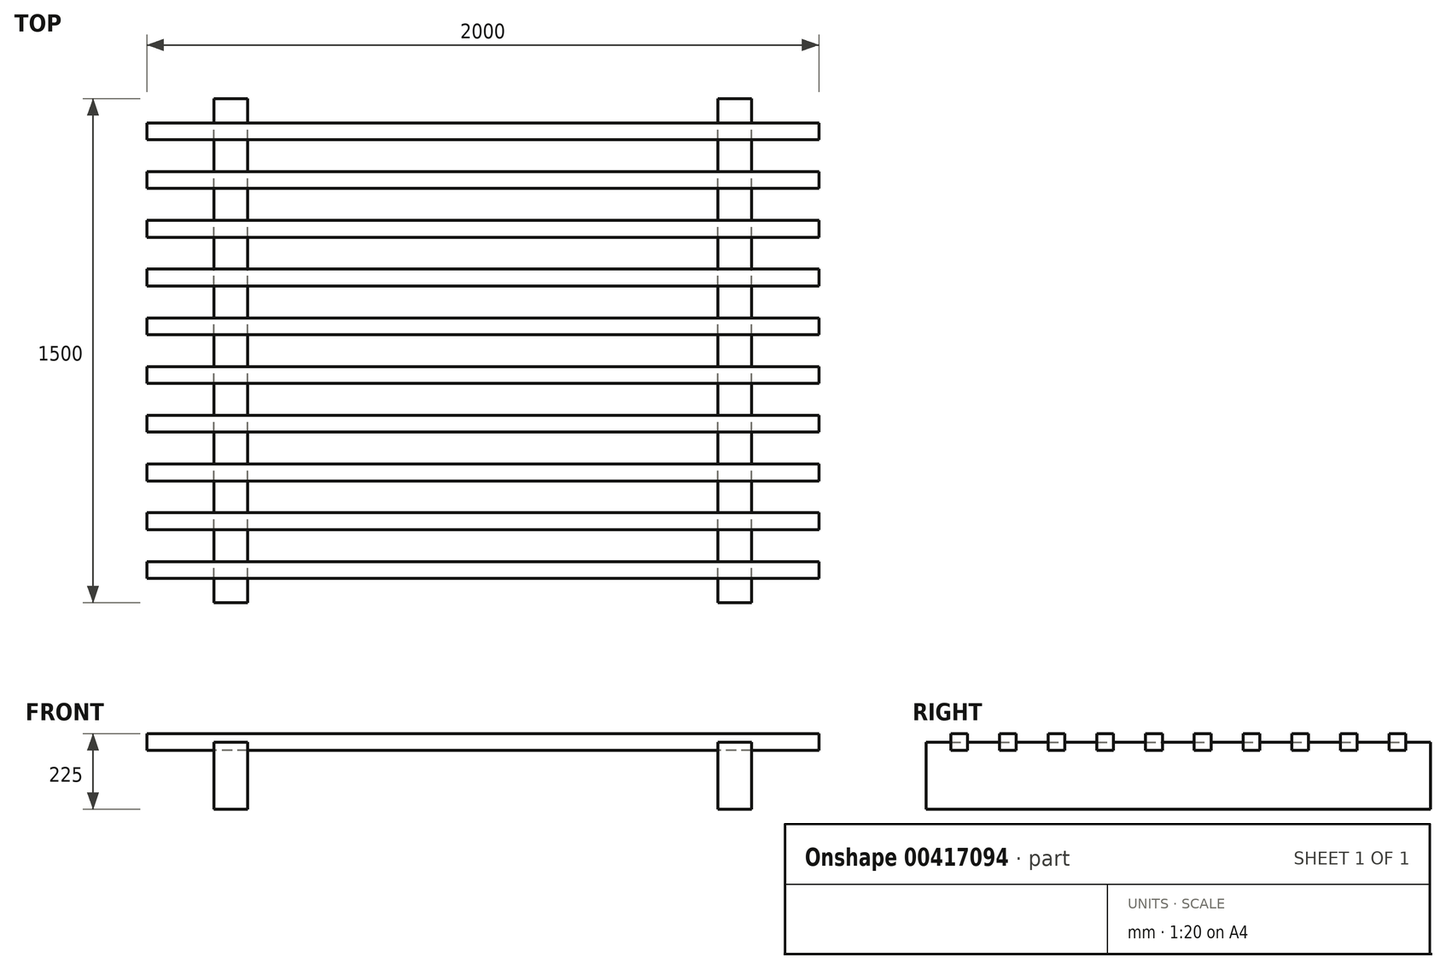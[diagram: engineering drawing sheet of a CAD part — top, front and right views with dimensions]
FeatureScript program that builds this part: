
annotation { "Feature Type Name" : "Feature", "Feature Type Description" : "" }
export const myFeature = defineFeature(function(context is Context, id is Id, definition is map)
    precondition{}
    {
        {
            var Q0;
            Q0=qCreatedBy(makeId("Top.planeOp"),FACE);
            var sketch = newSketch(context, id + "F0", { "sketchPlane" : qUnion([Q0])});
            skLineSegment(sketch, "E0.bottom", {"start": v(0, 0) * mm, "end": v(100, 0) * mm});
            skLineSegment(sketch, "E0.top", {"start": v(0, 1500) * mm, "end": v(100, 1500) * mm});
            skLineSegment(sketch, "E0.left", {"start": v(0, 0) * mm, "end": v(0, 1500) * mm});
            skLineSegment(sketch, "E0.right", {"start": v(100, 0) * mm, "end": v(100, 1500) * mm});
            skLineSegment(sketch, "E1.bottom", {"start": v(1500, 0) * mm, "end": v(1600, 0) * mm});
            skLineSegment(sketch, "E1.top", {"start": v(1500, 1500) * mm, "end": v(1600, 1500) * mm});
            skLineSegment(sketch, "E1.left", {"start": v(1500, 0) * mm, "end": v(1500, 1500) * mm});
            skLineSegment(sketch, "E1.right", {"start": v(1600, 0) * mm, "end": v(1600, 1500) * mm});
            skSolve(sketch);
        }
        {
            var Q0;
            Q0 = qSketchRegion(id + "F0", true);
            extrude(context, id + "F1", {"entities" : qUnion([Q0]), "depth" : 200 * mm});
        }
        {
            var Q0;
            Q0=makeQuery(id+"F1.opExtrude","SWEPT_FACE",FACE,{"disambiguationData":[OSD([sQuery(id+"F0.wireOp",EDGE,"E0.left")])]});
            cPlane(context, id + "F2", {"entities" : qUnion([Q0]), "cplaneType" : CPlaneType.OFFSET, "offset" : 200 * mm, "width" : 150 * mm, "height" : 150 * mm});
        }
        {
            var Q0;
            Q0=qCreatedBy(id+"F2.planeOp",FACE);
            var sketch = newSketch(context, id + "F3", { "sketchPlane" : qUnion([Q0])});
            skLineSegment(sketch, "E2.bottom", {"start": v(-1427.5, 225) * mm, "end": v(-1377.5, 225) * mm});
            skLineSegment(sketch, "E2.top", {"start": v(-1427.5, 175) * mm, "end": v(-1377.5, 175) * mm});
            skLineSegment(sketch, "E2.left", {"start": v(-1427.5, 225) * mm, "end": v(-1427.5, 175) * mm});
            skLineSegment(sketch, "E2.right", {"start": v(-1377.5, 225) * mm, "end": v(-1377.5, 175) * mm});
            skLineSegment(sketch, "E3.1.0.0", {"start": v(-1232.5, 225) * mm, "end": v(-1232.5, 175) * mm});
            skLineSegment(sketch, "E3.1.0.1", {"start": v(-1282.5, 225) * mm, "end": v(-1282.5, 175) * mm});
            skLineSegment(sketch, "E3.1.0.2", {"start": v(-1282.5, 175) * mm, "end": v(-1232.5, 175) * mm});
            skLineSegment(sketch, "E3.1.0.3", {"start": v(-1282.5, 225) * mm, "end": v(-1232.5, 225) * mm});
            skLineSegment(sketch, "E3.2.0.0", {"start": v(-1087.5, 225) * mm, "end": v(-1087.5, 175) * mm});
            skLineSegment(sketch, "E3.2.0.1", {"start": v(-1137.5, 225) * mm, "end": v(-1137.5, 175) * mm});
            skLineSegment(sketch, "E3.2.0.2", {"start": v(-1137.5, 175) * mm, "end": v(-1087.5, 175) * mm});
            skLineSegment(sketch, "E3.2.0.3", {"start": v(-1137.5, 225) * mm, "end": v(-1087.5, 225) * mm});
            skLineSegment(sketch, "E3.3.0.0", {"start": v(-942.5, 225) * mm, "end": v(-942.5, 175) * mm});
            skLineSegment(sketch, "E3.3.0.1", {"start": v(-992.5, 225) * mm, "end": v(-992.5, 175) * mm});
            skLineSegment(sketch, "E3.3.0.2", {"start": v(-992.5, 175) * mm, "end": v(-942.5, 175) * mm});
            skLineSegment(sketch, "E3.3.0.3", {"start": v(-992.5, 225) * mm, "end": v(-942.5, 225) * mm});
            skLineSegment(sketch, "E3.4.0.0", {"start": v(-797.5, 225) * mm, "end": v(-797.5, 175) * mm});
            skLineSegment(sketch, "E3.4.0.1", {"start": v(-847.5, 225) * mm, "end": v(-847.5, 175) * mm});
            skLineSegment(sketch, "E3.4.0.2", {"start": v(-847.5, 175) * mm, "end": v(-797.5, 175) * mm});
            skLineSegment(sketch, "E3.4.0.3", {"start": v(-847.5, 225) * mm, "end": v(-797.5, 225) * mm});
            skLineSegment(sketch, "E3.5.0.0", {"start": v(-652.5, 225) * mm, "end": v(-652.5, 175) * mm});
            skLineSegment(sketch, "E3.5.0.1", {"start": v(-702.5, 225) * mm, "end": v(-702.5, 175) * mm});
            skLineSegment(sketch, "E3.5.0.2", {"start": v(-702.5, 175) * mm, "end": v(-652.5, 175) * mm});
            skLineSegment(sketch, "E3.5.0.3", {"start": v(-702.5, 225) * mm, "end": v(-652.5, 225) * mm});
            skLineSegment(sketch, "E3.6.0.0", {"start": v(-507.5, 225) * mm, "end": v(-507.5, 175) * mm});
            skLineSegment(sketch, "E3.6.0.1", {"start": v(-557.5, 225) * mm, "end": v(-557.5, 175) * mm});
            skLineSegment(sketch, "E3.6.0.2", {"start": v(-557.5, 175) * mm, "end": v(-507.5, 175) * mm});
            skLineSegment(sketch, "E3.6.0.3", {"start": v(-557.5, 225) * mm, "end": v(-507.5, 225) * mm});
            skLineSegment(sketch, "E3.7.0.0", {"start": v(-362.5, 225) * mm, "end": v(-362.5, 175) * mm});
            skLineSegment(sketch, "E3.7.0.1", {"start": v(-412.5, 225) * mm, "end": v(-412.5, 175) * mm});
            skLineSegment(sketch, "E3.7.0.2", {"start": v(-412.5, 175) * mm, "end": v(-362.5, 175) * mm});
            skLineSegment(sketch, "E3.7.0.3", {"start": v(-412.5, 225) * mm, "end": v(-362.5, 225) * mm});
            skLineSegment(sketch, "E3.8.0.0", {"start": v(-217.5, 225) * mm, "end": v(-217.5, 175) * mm});
            skLineSegment(sketch, "E3.8.0.1", {"start": v(-267.5, 225) * mm, "end": v(-267.5, 175) * mm});
            skLineSegment(sketch, "E3.8.0.2", {"start": v(-267.5, 175) * mm, "end": v(-217.5, 175) * mm});
            skLineSegment(sketch, "E3.8.0.3", {"start": v(-267.5, 225) * mm, "end": v(-217.5, 225) * mm});
            skLineSegment(sketch, "E3.9.0.0", {"start": v(-72.5, 225) * mm, "end": v(-72.5, 175) * mm});
            skLineSegment(sketch, "E3.9.0.1", {"start": v(-122.5, 225) * mm, "end": v(-122.5, 175) * mm});
            skLineSegment(sketch, "E3.9.0.2", {"start": v(-122.5, 175) * mm, "end": v(-72.5, 175) * mm});
            skLineSegment(sketch, "E3.9.0.3", {"start": v(-122.5, 225) * mm, "end": v(-72.5, 225) * mm});
            skLineSegment(sketch, "E3.direction1", {"start": v(-1427.5, 175) * mm, "end": v(-1282.5, 175) * mm, "construction": true});
            skSolve(sketch);
        }
        {
            var Q0;
            Q0 = qSketchRegion(id + "F3", true);
            extrude(context, id + "F4", {"entities" : qUnion([Q0]), "oppositeDirection" : true, "depth" : 2000 * mm});
        }
    });
